# Revit family: Hager-WITTY PRO ON PEDESTAL-fr-FR-FR
name_source: partatom
category: Electrical Fixtures
units: mm (PartAtom-declared; Revit-internal decimal feet)

## family parameters
Always vertical = Yes
Cut with Voids When Loaded = No
Maintain Annotation Orientation = No
Part Type = Normal
Room Calculation Point = No
Round Connector Dimension = Use Diameter
Shared = No
Work Plane-Based = No

## types (2) — shared parameters
BC_METADATA = {"ObjectGuid":"309c69a2-f6b5-4723-8d44-322179afe64e","ModelGuid":"04826155-e6fb-4358-826f-cf700e871803","VariantGuid":"d0dc6e8a-84e1-41b3-adf0-62c97217fd0d","Revision":"#2","VariantName":"REF 1"}
BC_MODEL_ID = 1528400
BC_OBJECT_ID = 511122
BC_OBJECT_VERSION = #1
Code hager = ADD_EC002883_ECVS_WO
EF000003 - mode de pose = montage mural
EF000008 - largeur = 250 mm  [stored 0.82021 ft]
EF000040 - hauteur = 370 mm  [stored 1.21391 ft]
EF000049 - profondeur = 150 mm
EF000458 - avec affichage = No
EF001596 - matériau du boîtier/corps = plastique
EF002136 - puissance de raccordement nominale = 22000 W
EF003840 - tension d'entrée = 400 V
EF004293 - indice de protection contre les chocs (IK) = IK10
EF005455 - fréquence = 50/60 Hz
EF005474 - indice de protection (IP) = IP55
EF007001 - tension de sortie CC = 0 V
EF007353 - courant de sortie max. CC = 0 A
EF009078 - nombre de points de chargement = 1
EF009089 - avec boîte de raccordement domestique = No
EF009300 - puissance max. par point de chargement = 22000 W
EF009305 - nombre de prises de charge type 2 = 1
EF009313 - avec compteur d'énergie = Yes
EF009314 - avec disjoncteur de protection = No
EF009547 - LTE = No
EF011072 - compatible IFTTT = No
EF012191 - avec lecteur de carte RFID intégré = Yes
EF012361 - NFC (Near Field Communication) = No
EF013154 - connectable via Wi-Fi = Yes
EF014925 - compatible avec Apple HomeKit = No
EF014926 - compatible avec Google Assistant = No
EF014927 - compatible avec Amazon Alexa = No
EF016385 - standard radio 5G = No
EF017508 - mise en réseau en maître = No
EF017509 - détection de courant résiduel DC = No
EF017511 - avec interrupteur à clé = No
EF017512 - export de l'historique de charge = Yes
EF017513 - version protocole OCPP (Open Charge Point Protocol) = 1.6
EF017515 - Plug & Charge selon ISO 15118 = No
EF017517 - mise en réseau comme extension = No
EF017663 - câble de recharge avec verrouillage permanent sur la station de charge = No
EF017664 - mise réseau via LAN = Yes
EF017665 - compteur électrique compatible avec directive MID = Yes
EF017668 - gestion intégrée de la charge statique = Yes
EF017669 - convient pour une charge dynamique = Yes
EF017672 - backend compris dans la livraison = No
EF017972 - utilisation et configuration via application mobile = Yes
EF025053 - exécution raccord côté installation = triphasé
EFDE0066 - conforme à la législation sur l'étalonnage = No
ETIM class code = EC002883
ETIM class name = Charging device E-Mobility
HG000003-Range = WITTY PRO
HG000065-With socket TE = No
HG000099-Onfly Template ID = WittyOne_EVCS_On_Pedestal
Manufacturer = hager France
Name = WITTY PRO ON PEDESTAL-FR
Name BIM&CO = Electricity
Name hager = ADD_ChargingStation_EC002883
Reference description = ECVS Witty 1x22kW 3P T2S
zero-valued in all types: Default Elevation, EF006577 - nombre de prises CEE, EF008200 - section de conducteur connectable, EF009091 - nombre d'interrupteurs différentiels type A, EF009092 - nombre d'interrupteurs différentiels type B, EF009301 - nombre de coupleurs de charge type 1, EF009302 - nombre de coupleurs de charge type 1 CCS, EF009303 - nombre de coupleurs de charge type 2, EF009304 - nombre de coupleurs de charge type 2 CCS, EF009306 - nombre de coupleurs de charge GB CA, EF009307 - nombre de coupleurs de charge GB CC, EF009308 - nombre de prises de charge GB, EF009309 - nombre de prises de charge type 3, EF009310 - nombre de coupleurs de charge CHAdeMO, EF009311 - nombre de prises de courant domestiques, EF014895 - longueur du câble de charge

## per-type parameters (varying)
| type | BC_VARIANT_ID | HG000004-Manufacturer reference |
| WITTY PRO-1x22kW-3P-XVL122SLM-DOUBLE STATION-RECTANGULAR PEDESTAL | 1164514 | XVL122SLM / XVL122SLM / XVA135 |
| WITTY PRO-1x22kW-3P-XVL122SLM-RECTANGULAR PEDESTAL | 1164515 | XVL122SLM / XVA130 |

note: column(s) folded — value = type name in every type: Reference

note: [stored X ft] marks values corroborated as IEEE doubles in the binary element streams (Revit-internal decimal feet)
